# Revit family: Capacitive_touch_switch-TMDP8-AA_-AW_-PA_-PS_PW
name_source: partatom
category: Equipos especializados
revit_build: Autodesk Revit 2018 (Build: 20170927_1515(x64)
units: mm (PartAtom-declared; Revit-internal decimal feet)

## family parameters
Anfitrión = Cara
Compartido = No
Corte con vacíos al cargar = No
Cota de conector redondo = Diámetro de uso
Punto de cálculo de habitación = No
Tipo de pieza = Normal

## types (12) — shared parameters
Analog/digital inputs = 2
BCU = Integrated KNX BCU
Comentarios de tipo = Completely customized image for printout glass through web application
Complementary characteristics = Class B
Connection type = Typical TP1 bus connector for rigid cable 0.80 mm diameter
Degree of protection = IP20, clean environment
Depth = 12 mm  [stored 0.0393701 ft]
Depth_total = 25 mm  [stored 0.082021 ft]
Descripción = KNX Capacitive Touch Switch with 8 buttons
Device action type = Type 1
Electrical stress period = Long
Elevación por defecto = 1219 mm
External power supply connection = No power supply different from the bus needed
Fabricante = Zennio Avance y Tecnología, S.L.
Fit = Magnetic fit. Metallic stand included
Height = 123 mm
Maximum consumption 24 VDC = 8,5mA
Maximum consumption 29 VDC typical = 7mA
Nota clave = 8 main touch areas and 5 auxiliary touch areas. State LED indicators with custom luminosity
Operating humidity = 30 to 85% RH (no condensation)
Operating temperature = 5ºC to +40ºC
Operation type = Continuous operation
Orientation = Vertical or horizontal position
PCB CTI index = 175 V
Product Page URL = http://www.zennio.com
Protection class = III
Storage humidity = 30 to 85% RH (no condensation)
Storage temperature = -20ºC to +60ºC
Temperature sensor = Built-in temperature sensor
Thermostats = 1
URL = http://www.zennio.com
Voltage range (KNX supply) = 21...31VDC
Voltage typical (KNX supply) = 29VDC SELV
Width = 90 mm

## per-type parameters (varying)
| type | Constraints | Constraints2 | Constraints3 | Flush | Frame material | Housing material | Surface | Weight |
| ZVI-TMDP8-PA_surface | 2 | 1 | 1 | No | Polycarbonate frame - Anthracite | PC/ABS FR V0 halogen free - Anthracite | Sí | 140g |
| ZVI-TMDP8-PA_flush | 2 | 1 | 2 | Sí | Polycarbonate frame - Anthracite | PC/ABS FR V0 halogen free - Anthracite | No | 140g |
| ZVI-TMDP8-AA_surface | 1 | 1 | 1 | No | Aluminium frame | PC/ABS FR V0 halogen free - Anthracite | Sí | 180g |
| ZVI-TMDP8-AA_flush | 1 | 1 | 2 | Sí | Aluminium frame | PC/ABS FR V0 halogen free - Anthracite | No | 180g |
| ZVI-TMDP8-AW_surface | 1 | 3 | 1 | No | Aluminium frame | PC/ABS FR V0 halogen free - White | Sí | 180g |
| ZVI-TMDP8-PW_surface | 2 | 3 | 1 | No | Polycarbonate frame - White | PC/ABS FR V0 halogen free - White | Sí | 140g |
| ZVI-TMDP8-AW_flush | 1 | 3 | 2 | Sí | Aluminium frame | PC/ABS FR V0 halogen free - White | No | 180g |
| ZVI-TMDP8-PW_flush | 2 | 3 | 2 | Sí | Polycarbonate frame - White | PC/ABS FR V0 halogen free - White | No | 140g |
| ZVI-TMDP8_surface | 1 | 2 | 1 | No | Aluminium frame | PC/ABS FR V0 halogen free - Silver | Sí | 180g |
| ZVI-TMDP8-P_surface | 2 | 2 | 1 | No | Polycarbonate frame - Silver | PC/ABS FR V0 halogen free - Silver | Sí | 140g |
| ZVI-TMDP8_flush | 1 | 2 | 2 | Sí | Aluminium frame | PC/ABS FR V0 halogen free - Silver | No | 180g |
| ZVI-TMDP8-P_flush | 2 | 2 | 2 | Sí | Polycarbonate frame - Silver | PC/ABS FR V0 halogen free - Silver | No | 140g |

note: column(s) folded — value = type name in every type: Modelo

note: [stored X ft] marks values corroborated as IEEE doubles in the binary element streams (Revit-internal decimal feet)

## geometry (parser evidence)
native form markers: Sweep x2
no freeform markers — native parametric forms only
